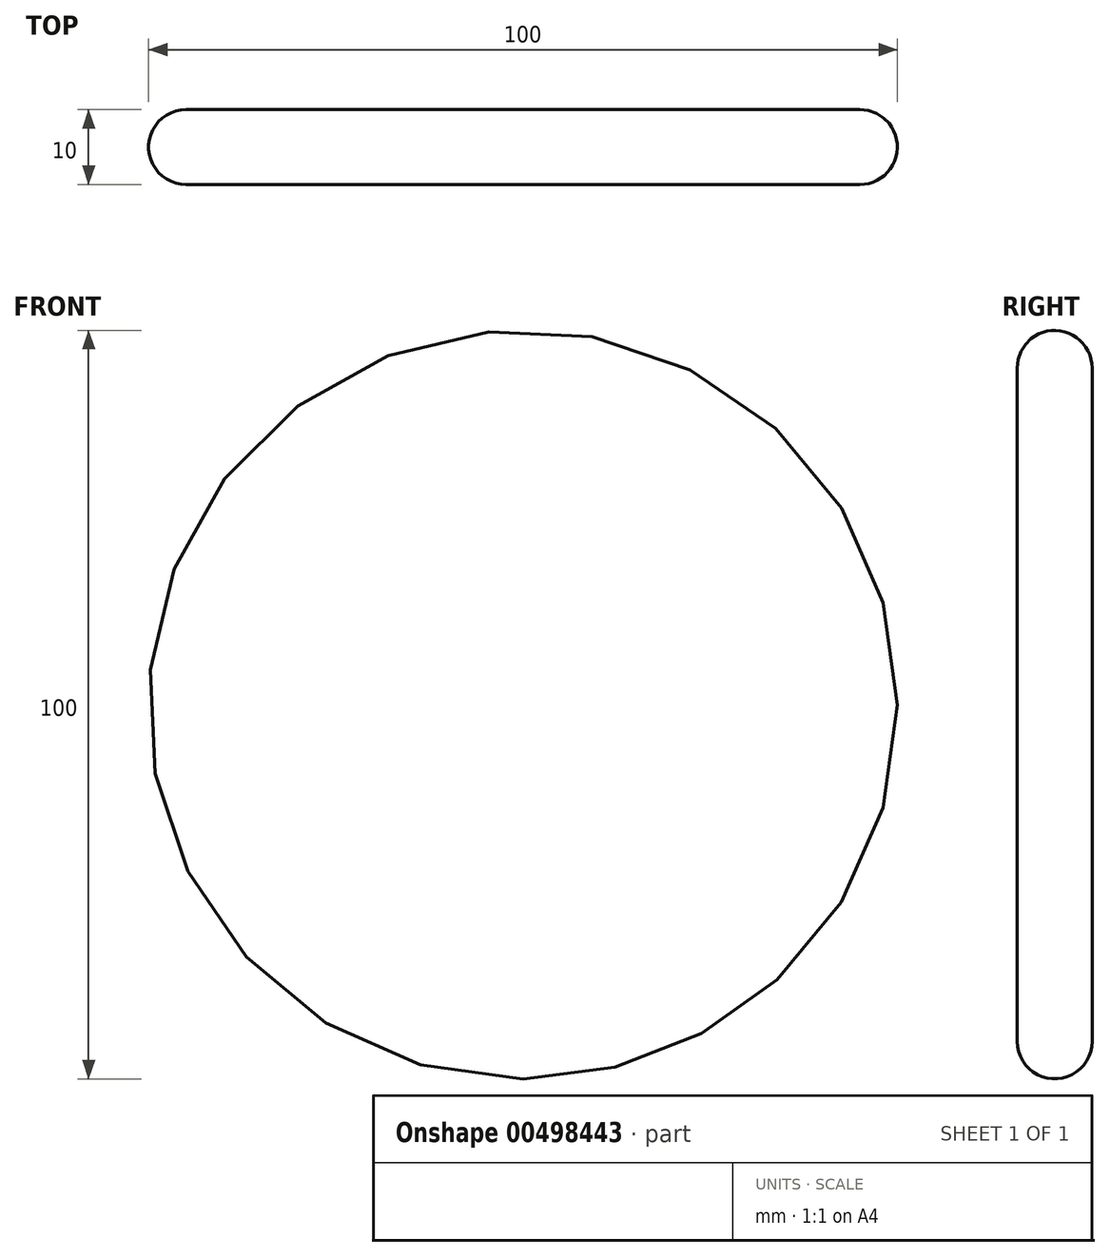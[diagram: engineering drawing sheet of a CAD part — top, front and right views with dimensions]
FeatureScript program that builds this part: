
annotation { "Feature Type Name" : "Feature", "Feature Type Description" : "" }
export const myFeature = defineFeature(function(context is Context, id is Id, definition is map)
    precondition{}
    {
        {
            var Q0;
            Q0=qCreatedBy(makeId("Front.planeOp"),FACE);
            var sketch = newSketch(context, id + "F0", { "sketchPlane" : qUnion([Q0])});
            skCircle(sketch, "E0", {"center": v(0, 0) * mm, "radius": 50 * mm});
            skSolve(sketch);
        }
        {
            var Q0;
            Q0 = qSketchRegion(id + "F0", true);
            extrude(context, id + "F1", {"entities" : qUnion([Q0]), "depth" : 10 * mm});
        }
        {
            var Q0;
            Q0=makeQuery(id+"F1.opExtrude","CAP_EDGE",EDGE,{"disambiguationData":[OSD([sQuery(id+"F0.wireOp",EDGE,"E0")])],"isStart":true});
            fillet(context, id + "F2", {"entities" : qUnion([Q0]), "radius" : 5 * mm, "tangentPropagation" : true, "allowEdgeOverflow" : false});
        }
        {
            var Q0;
            Q0=makeQuery(id+"F1.opExtrude","CAP_EDGE",EDGE,{"disambiguationData":[OSD([sQuery(id+"F0.wireOp",EDGE,"E0")])],"isStart":false});
            var Q1;
            Q1=makeQuery(id+"F1.opExtrude","SWEPT_FACE",FACE,{"disambiguationData":[OSD([sQuery(id+"F0.wireOp",EDGE,"E0")])]});
            fillet(context, id + "F3", {"entities" : qUnion([Q0, Q1]), "radius" : 5 * mm, "tangentPropagation" : true, "allowEdgeOverflow" : false});
        }
    });
